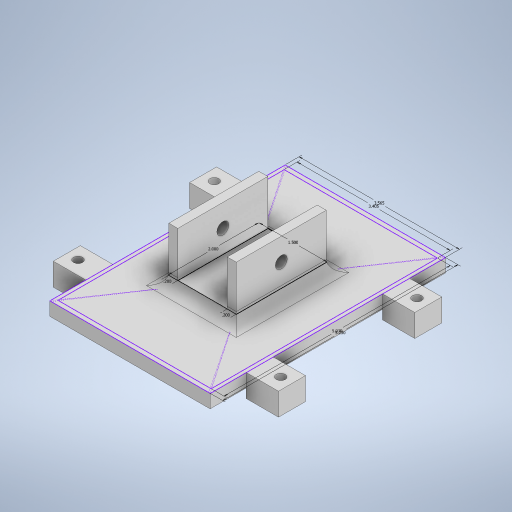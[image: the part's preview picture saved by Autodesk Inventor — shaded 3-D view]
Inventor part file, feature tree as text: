
AUTODESK INVENTOR PART (.ipt)
format: ipt  version: 2024.1 (Build 281209000, 209)  size: 382,464 bytes
history: native  units: in
note: dims shown in document units (in); Inventor stores cm internally (conversion verified against a paired STEP export)
features: extrude x5, sketch x3, hole x2, fillet x1, projected_geometry x1
ambient origin geometry x8: Origin, YZ Plane, XZ Plane, XY Plane, X Axis, Y Axis, Z Axis, Center Point
bodies: Solid1 (feature_tree)
feature tree (12):
  extrude  "Extrusion1"  Depth=2.0in
  extrude  "Extrusion2"  Depth=0.2in
  hole  "Hole1"  [1 undecoded]
  sketch  "Sketch3"  dims[d0=1.5in d1=2.0in]
  extrude  "Extrusion3"  Depth=0.5in
  extrude  "Extrusion4"  Depth=3.4054in
  fillet  "Fillet1"  Radius=5.0299in
  extrude  "Extrusion5"  Depth=5.23in
  hole  "Hole3"  [1 undecoded]
  projected_geometry  "Projected Loop1"
  sketch  "Sketch4"  dims[d2=0.2in d3=0.2in]
  sketch  "Sketch6"  dims[d4=1.0in d5=0.0in d6=0.2in d7=0.0in d8=0.5in d9=0.266in d10=0.75in d11=0.438in d12=0.25in d13=0.5635in d14=1.0in d15=0.8108in d16=3.4054in d17=5.0299in d18=5.23in d19=3.565in d20=0.1in d21=0.0in d22=0.3in d23=0.0in d24=0.25in d25=1.0in d26=0.5in d27=1.0in d28=0.5in d29=0.5in d30=0.0in d38=1.0in d39=1.0in d40=1.0in d41=90.0deg d42=1.0in d43=1.6in d44=0.6in d45=1.6in d46=0.6in d47=1.6in d48=0.6in d49=1.6in d50=0.6in d51=0.55in d52=0.25in d53=0.25in d54=0.25in d55=0.2031in d56=0.75in d57=0.438in d58=0.25in d59=0.5635in d60=1.0in d61=0.8108in]
note: 2 required parameter values undecoded (feature->parameter linkage not recoverable at this tier; creation-order binding heuristic only, values carry confidence <= 0.55)
